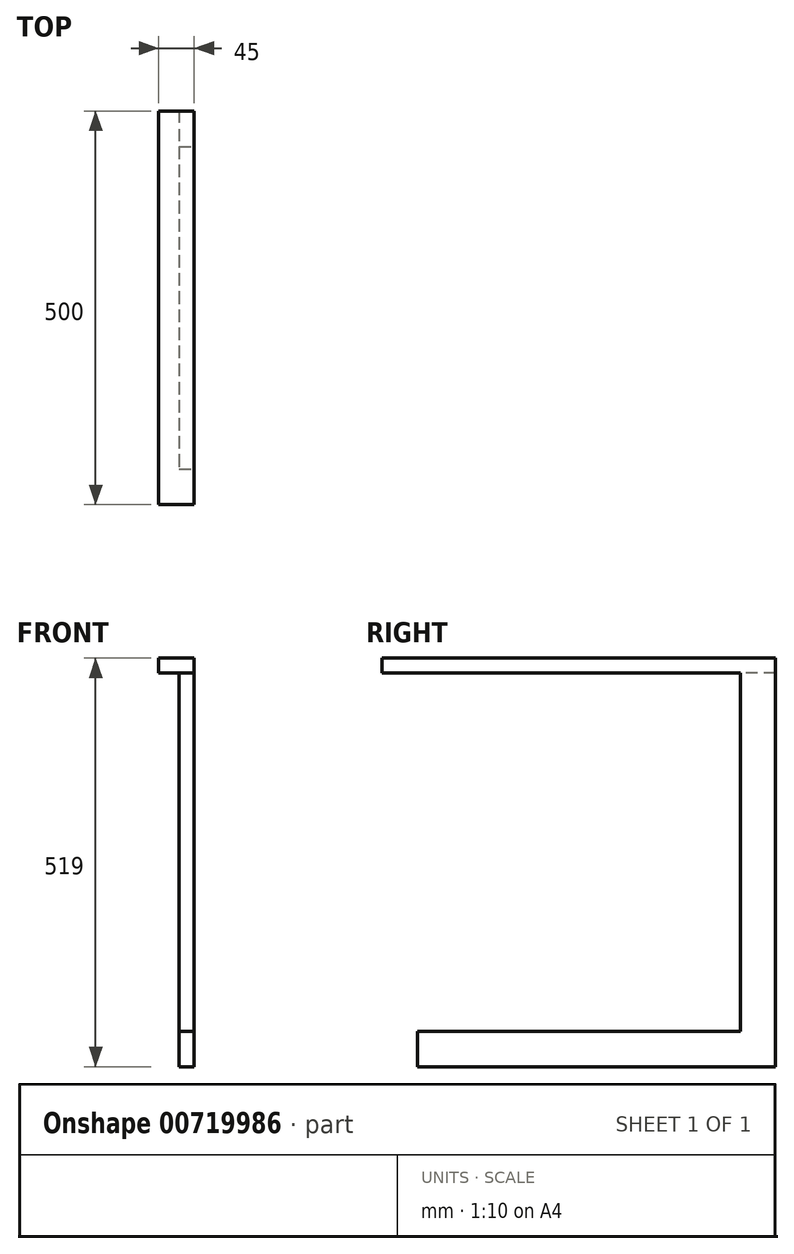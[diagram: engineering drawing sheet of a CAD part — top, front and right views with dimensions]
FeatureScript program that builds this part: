
annotation { "Feature Type Name" : "Feature", "Feature Type Description" : "" }
export const myFeature = defineFeature(function(context is Context, id is Id, definition is map)
    precondition{}
    {
        {
            var Q0;
            Q0=qCreatedBy(makeId("Right.planeOp"),FACE);
            var sketch = newSketch(context, id + "F0", { "sketchPlane" : qUnion([Q0])});
            skLineSegment(sketch, "E0.bottom", {"start": v(250, -9.5) * mm, "end": v(-250, -9.5) * mm});
            skLineSegment(sketch, "E0.top", {"start": v(250, 9.5) * mm, "end": v(-250, 9.5) * mm});
            skLineSegment(sketch, "E0.left", {"start": v(250, -9.5) * mm, "end": v(250, 9.5) * mm});
            skLineSegment(sketch, "E0.right", {"start": v(-250, -9.5) * mm, "end": v(-250, 9.5) * mm});
            skPoint(sketch, "E0.middle", {"position": v(0, 0) * mm});
            skLineSegment(sketch, "E1.bottom", {"start": v(-250, -9.5) * mm, "end": v(-205, -9.5) * mm});
            skLineSegment(sketch, "E1.top", {"start": v(-250, -509.5) * mm, "end": v(-205, -509.5) * mm});
            skLineSegment(sketch, "E1.left", {"start": v(-250, -9.5) * mm, "end": v(-250, -509.5) * mm});
            skLineSegment(sketch, "E1.right", {"start": v(-205, -9.5) * mm, "end": v(-205, -509.5) * mm});
            skLineSegment(sketch, "E2.bottom", {"start": v(250, -509.5) * mm, "end": v(205, -509.5) * mm});
            skLineSegment(sketch, "E2.top", {"start": v(250, -9.5) * mm, "end": v(205, -9.5) * mm});
            skLineSegment(sketch, "E2.left", {"start": v(250, -509.5) * mm, "end": v(250, -9.5) * mm});
            skLineSegment(sketch, "E2.right", {"start": v(205, -509.5) * mm, "end": v(205, -9.5) * mm});
            skLineSegment(sketch, "E3.bottom", {"start": v(205, -509.5) * mm, "end": v(-205, -509.5) * mm});
            skLineSegment(sketch, "E3.top", {"start": v(205, -464.5) * mm, "end": v(-205, -464.5) * mm});
            skLineSegment(sketch, "E3.left", {"start": v(205, -509.5) * mm, "end": v(205, -464.5) * mm});
            skLineSegment(sketch, "E3.right", {"start": v(-205, -509.5) * mm, "end": v(-205, -464.5) * mm});
            skSolve(sketch);
        }
        {
            var Q0;
            Q0=makeQuery(id+"F0.imprint","IMPRINT",FACE,{"disambiguationData":[TD([[makeQuery(id+"F0.imprint","IMPRINT",EDGE,{"derivedFrom":sQuery(id+"F0.wireOp",EDGE,"E1.bottom")}),-1.0]])]});
            var Q1;
            Q1=makeQuery(id+"F0.imprint","IMPRINT",FACE,{"disambiguationData":[TD([[makeQuery(id+"F0.imprint","IMPRINT",EDGE,{"derivedFrom":sQuery(id+"F0.wireOp",EDGE,"E2.bottom")}),-1.0]])]});
            var Q2;
            Q2=makeQuery(id+"F0.imprint","IMPRINT",FACE,{"disambiguationData":[TD([[makeQuery(id+"F0.imprint","IMPRINT",EDGE,{"derivedFrom":sQuery(id+"F0.wireOp",EDGE,"E3.bottom")}),-1.0]])]});
            extrude(context, id + "F1", {"entities" : qUnion([Q0, Q1, Q2]), "oppositeDirection" : true, "depth" : 19 * mm, "offsetDistance" : 25 * mm});
        }
        {
            var Q0;
            Q0=makeQuery(id+"F0.imprint","IMPRINT",FACE,{"disambiguationData":[TD([[makeQuery(id+"F0.imprint","IMPRINT",EDGE,{"derivedFrom":sQuery(id+"F0.wireOp",EDGE,"E0.bottom")}),-1.0]])]});
            extrude(context, id + "F2", {"entities" : qUnion([Q0]), "operationType" : NewBodyOperationType.ADD, "oppositeDirection" : true, "depth" : 45 * mm, "offsetDistance" : 25 * mm});
        }
    });
